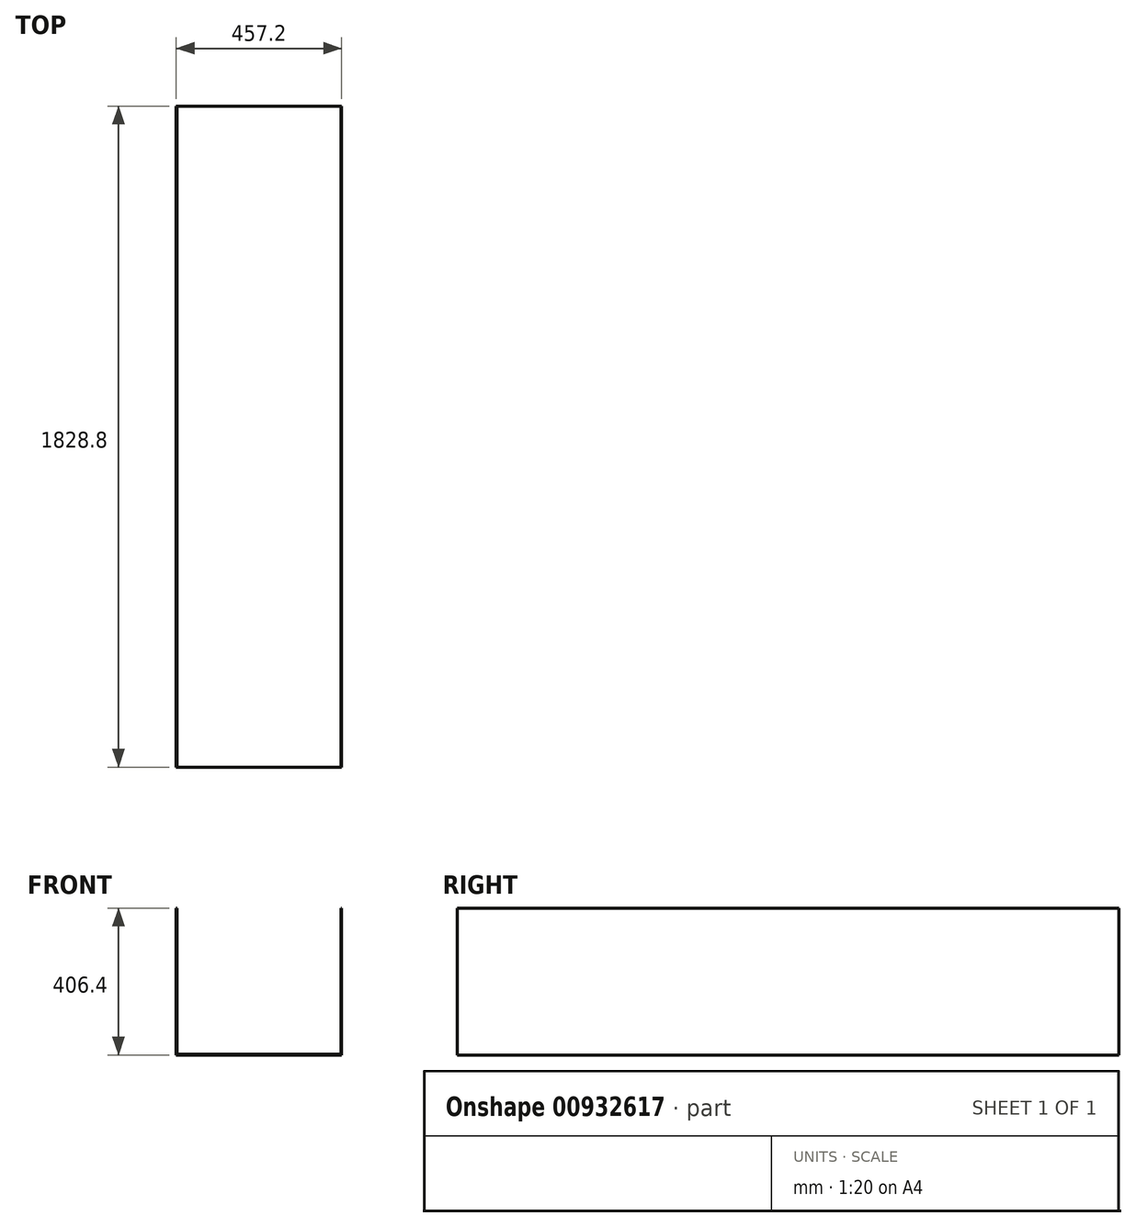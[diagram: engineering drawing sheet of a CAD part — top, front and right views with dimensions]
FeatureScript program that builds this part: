
annotation { "Feature Type Name" : "Feature", "Feature Type Description" : "" }
export const myFeature = defineFeature(function(context is Context, id is Id, definition is map)
    precondition{}
    {
        {
            var Q0;
            Q0=qCreatedBy(makeId("Front.planeOp"),FACE);
            var sketch = newSketch(context, id + "F0", { "sketchPlane" : qUnion([Q0])});
            skLineSegment(sketch, "E0", {"start": v(-228.6, 0) * mm, "end": v(228.6, 0) * mm});
            skLineSegment(sketch, "E1", {"start": v(-228.6, 0) * mm, "end": v(-228.6, 406.4) * mm});
            skLineSegment(sketch, "E2", {"start": v(228.6, 0) * mm, "end": v(228.6, 406.4) * mm});
            skLineSegment(sketch, "E3", {"start": v(-228.6, 406.4) * mm, "end": v(-227.1, 406.4) * mm});
            skLineSegment(sketch, "E4", {"start": v(-227.1, 406.4) * mm, "end": v(-227.1, 1.5) * mm});
            skLineSegment(sketch, "E5", {"start": v(-227.1, 1.5) * mm, "end": v(227.1, 1.5) * mm});
            skLineSegment(sketch, "E6", {"start": v(227.1, 1.5) * mm, "end": v(227.1, 406.4) * mm});
            skLineSegment(sketch, "E7", {"start": v(227.1, 406.4) * mm, "end": v(228.6, 406.4) * mm});
            skPoint(sketch, "E8.visualSharp", {"position": v(-227.1, 1.5) * mm});
            skLineSegment(sketch, "E8.filletArc", {"start": v(-227.1, 1.5) * mm, "end": v(-227.1, 1.5) * mm});
            skPoint(sketch, "E9.visualSharp", {"position": v(227.1, 1.5) * mm});
            skLineSegment(sketch, "E9.filletArc", {"start": v(227.1, 1.5) * mm, "end": v(227.1, 1.5) * mm});
            skSolve(sketch);
        }
        {
            var Q0;
            Q0=makeQuery(id+"F0.imprint","IMPRINT",FACE,{"disambiguationData":[TD([[makeQuery(id+"F0.imprint","IMPRINT",EDGE,{"derivedFrom":sQuery(id+"F0.wireOp",EDGE,"E0")}),1.0]])]});
            extrude(context, id + "F1", {"entities" : qUnion([Q0]), "endBound" : BoundingType.SYMMETRIC, "depth" : 1828.8 * mm, "offsetDistance" : 25.4 * mm});
        }
    });
